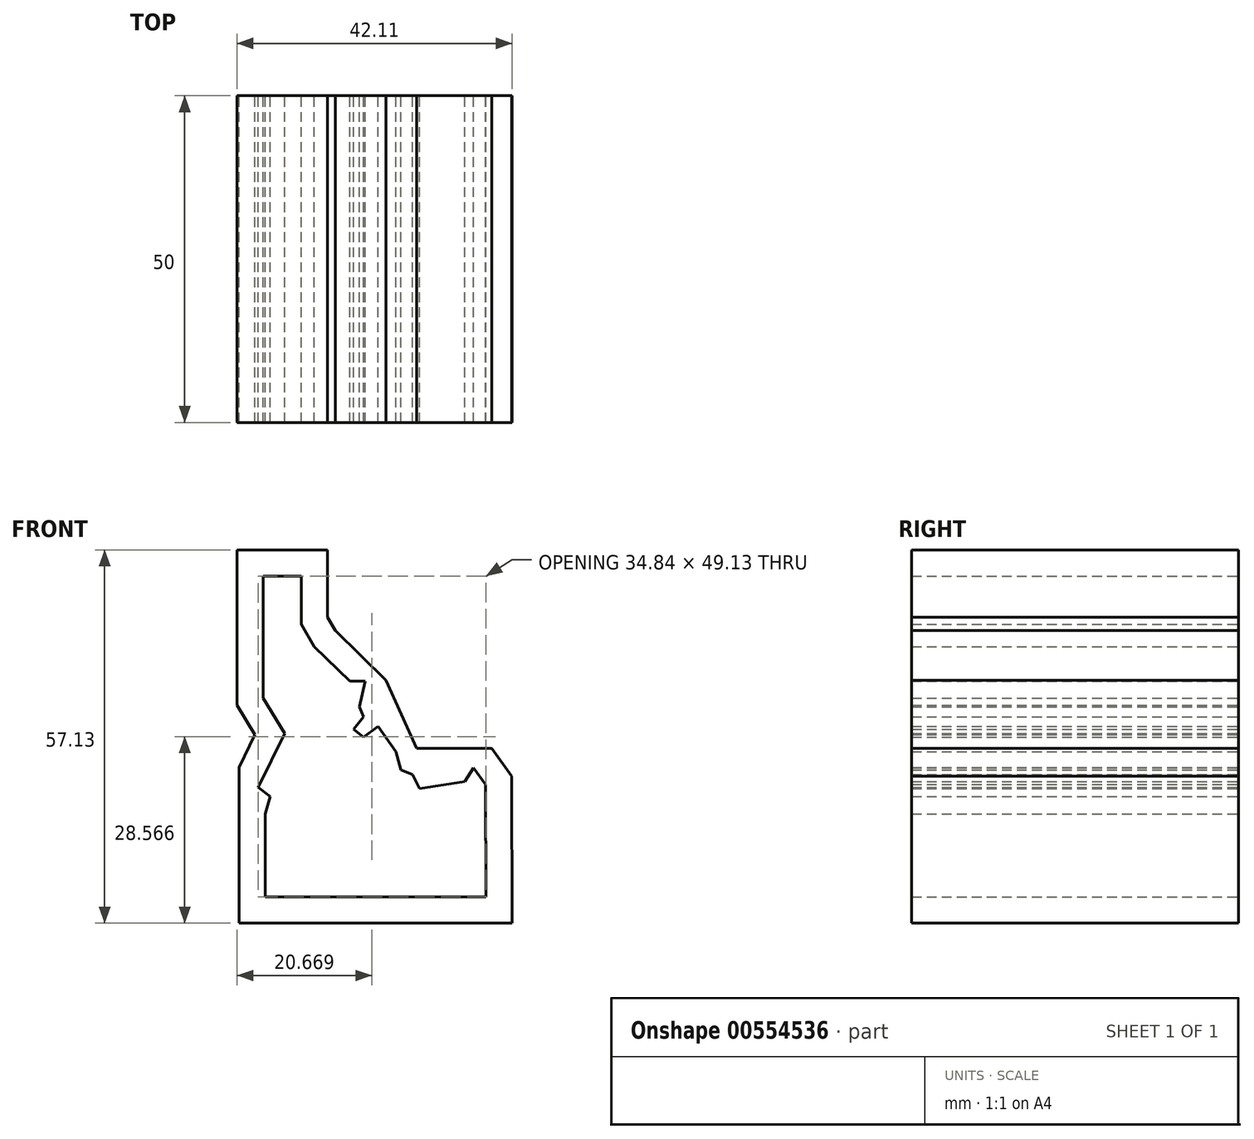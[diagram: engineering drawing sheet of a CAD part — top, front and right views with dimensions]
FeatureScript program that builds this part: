
annotation { "Feature Type Name" : "Feature", "Feature Type Description" : "" }
export const myFeature = defineFeature(function(context is Context, id is Id, definition is map)
    precondition{}
    {
        {
            var Q0;
            Q0=qCreatedBy(makeId("Front.planeOp"),FACE);
            var sketch = newSketch(context, id + "F0", { "sketchPlane" : qUnion([Q0])});
            skLineSegment(sketch, "E0", {"start": v(-0.99, 0.62) * mm, "end": v(-34.78, 0.62) * mm});
            skLineSegment(sketch, "E1", {"start": v(-34.78, 0.62) * mm, "end": v(-34.78, 13.33) * mm});
            skLineSegment(sketch, "E2", {"start": v(-34.78, 13.33) * mm, "end": v(-34.03, 16.04) * mm});
            skLineSegment(sketch, "E3", {"start": v(-34.03, 16.04) * mm, "end": v(-35.83, 17.4) * mm});
            skLineSegment(sketch, "E4", {"start": v(-35.83, 17.4) * mm, "end": v(-31.77, 25.67) * mm});
            skLineSegment(sketch, "E5", {"start": v(-31.77, 25.67) * mm, "end": v(-35.08, 31.09) * mm});
            skLineSegment(sketch, "E6", {"start": v(-35.08, 31.09) * mm, "end": v(-35.08, 49.75) * mm});
            skLineSegment(sketch, "E7", {"start": v(-35.08, 49.75) * mm, "end": v(-29.21, 49.75) * mm});
            skLineSegment(sketch, "E8", {"start": v(-29.21, 49.75) * mm, "end": v(-29.21, 42.38) * mm});
            skLineSegment(sketch, "E9", {"start": v(-29.21, 42.38) * mm, "end": v(-27.25, 38.92) * mm});
            skLineSegment(sketch, "E10", {"start": v(-27.25, 38.92) * mm, "end": v(-21.84, 33.65) * mm});
            skLineSegment(sketch, "E11", {"start": v(-21.84, 33.65) * mm, "end": v(-19.43, 33.65) * mm});
            skLineSegment(sketch, "E12", {"start": v(-19.43, 33.65) * mm, "end": v(-20.33, 29.73) * mm});
            skLineSegment(sketch, "E13", {"start": v(-20.33, 29.73) * mm, "end": v(-19.73, 28.23) * mm});
            skLineSegment(sketch, "E14", {"start": v(-19.73, 28.23) * mm, "end": v(-21.23, 26.27) * mm});
            skLineSegment(sketch, "E15", {"start": v(-21.23, 26.27) * mm, "end": v(-19.73, 25.11) * mm});
            skLineSegment(sketch, "E16", {"start": v(-19.73, 25.11) * mm, "end": v(-17.47, 26.72) * mm});
            skLineSegment(sketch, "E17", {"start": v(-17.47, 26.72) * mm, "end": v(-14.74, 22.9) * mm});
            skLineSegment(sketch, "E18", {"start": v(-14.74, 22.9) * mm, "end": v(-14, 20.1) * mm});
            skLineSegment(sketch, "E19", {"start": v(-14, 20.1) * mm, "end": v(-12.2, 19.35) * mm});
            skLineSegment(sketch, "E20", {"start": v(-12.2, 19.35) * mm, "end": v(-11.15, 17.24) * mm});
            skLineSegment(sketch, "E21", {"start": v(-11.15, 17.24) * mm, "end": v(-4.22, 18.3) * mm});
            skLineSegment(sketch, "E22", {"start": v(-4.22, 18.3) * mm, "end": v(-2.87, 20.4) * mm});
            skLineSegment(sketch, "E23", {"start": v(-2.87, 20.4) * mm, "end": v(-1.06, 17.84) * mm});
            skLineSegment(sketch, "E24", {"start": v(-1.06, 17.84) * mm, "end": v(-0.99, 0.62) * mm});
            skLineSegment(sketch, "E25.0", {"start": v(-39.08, 29.96) * mm, "end": v(-39.08, 53.75) * mm});
            skLineSegment(sketch, "E25.1", {"start": v(-36.33, 25.46) * mm, "end": v(-39.08, 29.96) * mm});
            skLineSegment(sketch, "E25.2", {"start": v(-38.78, 20.47) * mm, "end": v(-36.33, 25.46) * mm});
            skLineSegment(sketch, "E26.0", {"start": v(-24.05, 41.38) * mm, "end": v(-16.26, 33.8) * mm});
            skLineSegment(sketch, "E26.1", {"start": v(-25.21, 43.43) * mm, "end": v(-24.05, 41.38) * mm});
            skLineSegment(sketch, "E26.2", {"start": v(-25.21, 53.75) * mm, "end": v(-25.21, 43.43) * mm});
            skLineSegment(sketch, "E26.3", {"start": v(-39.08, 53.75) * mm, "end": v(-25.21, 53.75) * mm});
            skLineSegment(sketch, "E27.0", {"start": v(-38.78, -3.38) * mm, "end": v(-38.78, 20.47) * mm});
            skLineSegment(sketch, "E27.2", {"start": v(-0.1, 23.4) * mm, "end": v(2.93, 19.12) * mm});
            skLineSegment(sketch, "E27.3", {"start": v(2.93, 19.12) * mm, "end": v(3.03, -3.38) * mm});
            skLineSegment(sketch, "E27.4", {"start": v(3.03, -3.38) * mm, "end": v(-38.78, -3.38) * mm});
            skLineSegment(sketch, "E28", {"start": v(-11.6, 23.4) * mm, "end": v(-0.1, 23.4) * mm});
            skLineSegment(sketch, "E29", {"start": v(-16.26, 33.8) * mm, "end": v(-11.6, 23.4) * mm});
            skPoint(sketch, "E30", {"position": v(-5.7, 23.4) * mm});
            skPoint(sketch, "E31.orphan", {"position": v(-8.37, 19.25) * mm});
            skPoint(sketch, "E32.orphan", {"position": v(-3.03, 27.56) * mm});
            skSolve(sketch);
        }
        {
            var Q0;
            Q0 = qSketchRegion(id + "F0", true);
            extrude(context, id + "F1", {"entities" : qUnion([Q0]), "depth" : 50 * mm, "offsetDistance" : 25 * mm});
        }
    });
